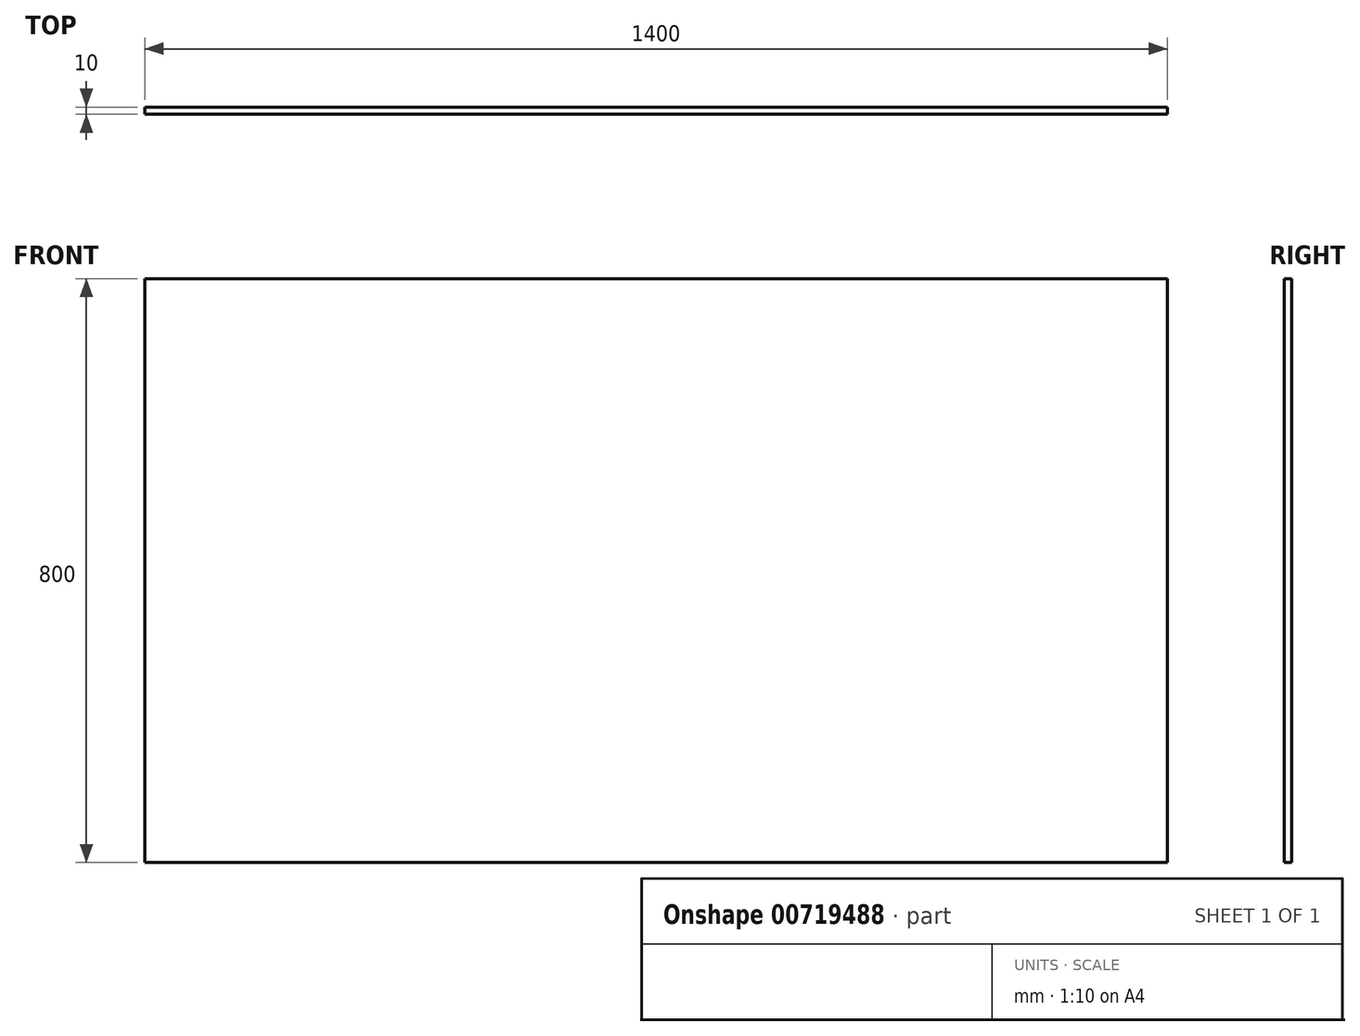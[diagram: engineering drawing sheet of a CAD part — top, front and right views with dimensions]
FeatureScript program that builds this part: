
annotation { "Feature Type Name" : "Feature", "Feature Type Description" : "" }
export const myFeature = defineFeature(function(context is Context, id is Id, definition is map)
    precondition{}
    {
        {
            var Q0;
            Q0=qCreatedBy(makeId("Front.planeOp"),FACE);
            var sketch = newSketch(context, id + "F0", { "sketchPlane" : qUnion([Q0])});
            skLineSegment(sketch, "E0.bottom", {"start": v(700, 400) * mm, "end": v(-700, 400) * mm});
            skLineSegment(sketch, "E0.top", {"start": v(700, -400) * mm, "end": v(-700, -400) * mm});
            skLineSegment(sketch, "E0.left", {"start": v(700, 400) * mm, "end": v(700, -400) * mm});
            skLineSegment(sketch, "E0.right", {"start": v(-700, 400) * mm, "end": v(-700, -400) * mm});
            skPoint(sketch, "E0.middle", {"position": v(0, 0) * mm});
            skSolve(sketch);
        }
        {
            var Q0;
            Q0=makeQuery(id+"F0.imprint","IMPRINT",FACE,{"disambiguationData":[TD([[makeQuery(id+"F0.imprint","IMPRINT",EDGE,{"derivedFrom":sQuery(id+"F0.wireOp",EDGE,"E0.bottom")}),1.0]])]});
            extrude(context, id + "F1", {"entities" : qUnion([Q0]), "depth" : 10 * mm, "offsetDistance" : 25 * mm});
        }
    });
